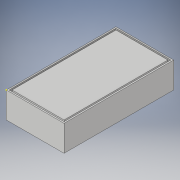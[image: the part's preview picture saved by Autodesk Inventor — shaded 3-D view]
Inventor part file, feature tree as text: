
AUTODESK INVENTOR PART (.ipt)
format: ipt  version: 2017 (Build 210142000, 142)  size: 184,320 bytes
history: native  units: in
note: dims shown in document units (in); Inventor stores cm internally (conversion verified against a paired STEP export)
features: extrude x4, sketch x4, plane x2, mirror x2, other x1
ambient origin geometry x8: Origin, YZ Plane, XZ Plane, XY Plane, X Axis, Y Axis, Z Axis, Center Point
bodies: Solid1 (feature_tree)
feature tree (13):
  extrude  "Extrusion1"  Depth=76.0in
  extrude  "Extrusion3"  Depth=1.0in
  extrude  "Extrusion4"  Depth=1.0in
  plane  "Work Plane1"
  mirror  "Mirror1"
  plane  "Work Plane2"
  extrude  "Extrusion5"  Depth=2.0in TaperAngle=0.0deg
  mirror  "Mirror2"
  sketch  "Sketch11"  dims[d16=1.0in d17=2.0in d18=0.0in d19=10.0in d20=18.0in d21=18.0in d22=10.0in d23=2.0in d24=0.0in d25=7.0in d26=7.0in d27=6.0in d28=2.0in d29=0.0in]
  sketch  "Sketch1"  dims[d0=40.0in d1=76.0in]
  sketch  "Sketch8"  dims[d2=18.0in d3=0.0in d13=1.0in]
  other  "InnerInset1"
  sketch  "Sketch10"  dims[d14=1.0in d15=1.0in]
